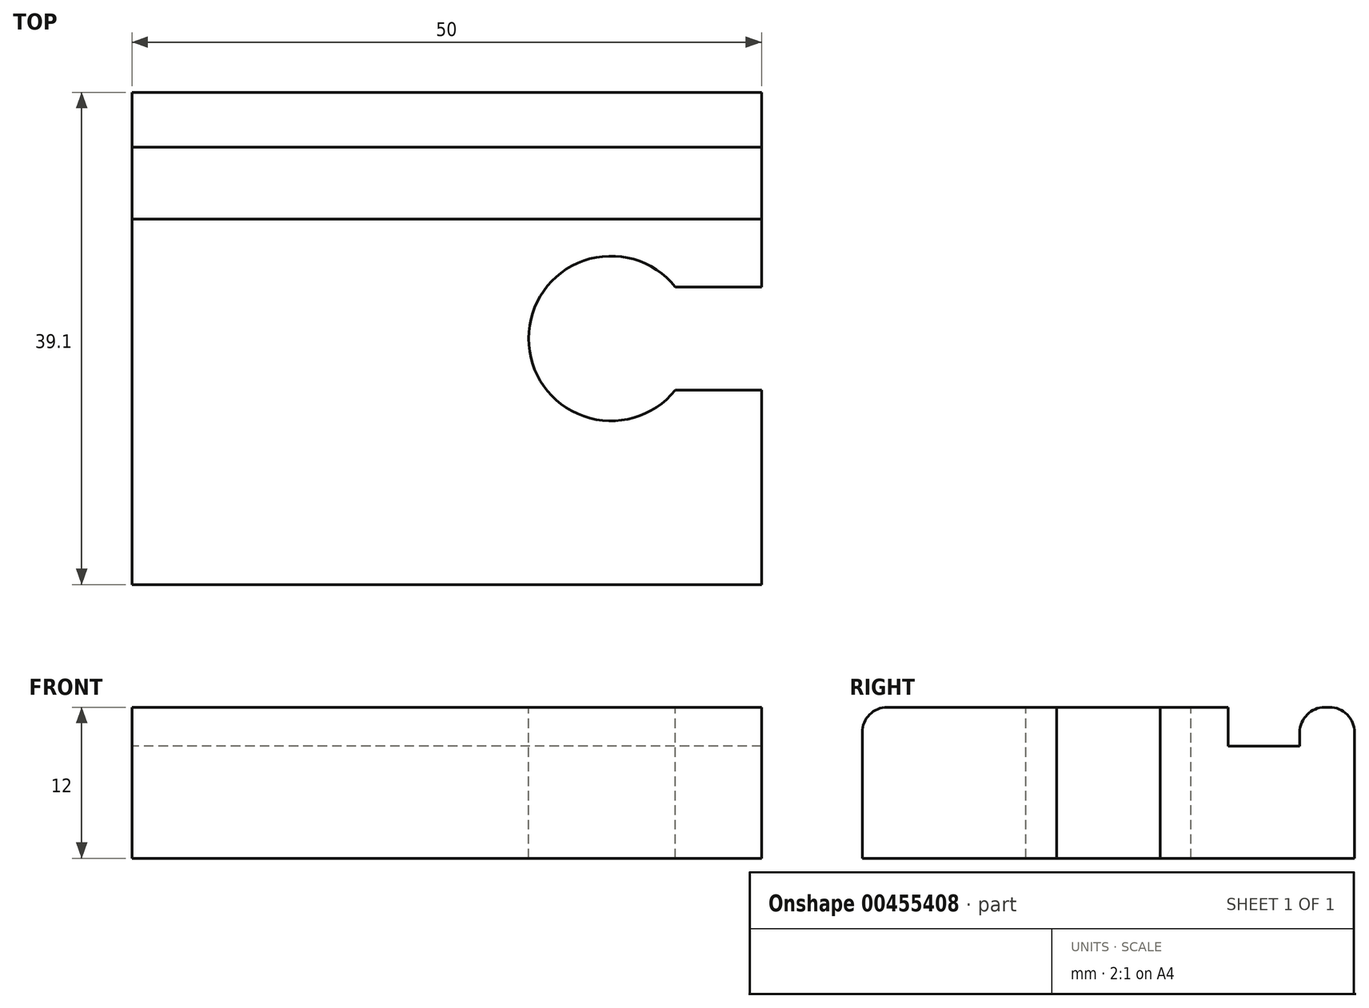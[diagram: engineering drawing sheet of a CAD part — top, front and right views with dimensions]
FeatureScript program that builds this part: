
annotation { "Feature Type Name" : "Feature", "Feature Type Description" : "" }
export const myFeature = defineFeature(function(context is Context, id is Id, definition is map)
    precondition{}
    {
        {
            var Q0;
            Q0=qCreatedBy(makeId("Top.planeOp"),FACE);
            var sketch = newSketch(context, id + "F0", { "sketchPlane" : qUnion([Q0])});
            skLineSegment(sketch, "E0.bottom", {"start": v(-25, 19.55) * mm, "end": v(25, 19.55) * mm});
            skLineSegment(sketch, "E0.top", {"start": v(-25, -19.55) * mm, "end": v(25, -19.55) * mm});
            skLineSegment(sketch, "E0.left", {"start": v(-25, 19.55) * mm, "end": v(-25, -19.55) * mm});
            skLineSegment(sketch, "E0.right", {"start": v(25, 19.55) * mm, "end": v(25, -19.55) * mm});
            skLineSegment(sketch, "E1", {"start": v(25, 0) * mm, "end": v(-25, 0) * mm, "construction": true});
            skLineSegment(sketch, "E2", {"start": v(0, 19.55) * mm, "end": v(0, -19.55) * mm, "construction": true});
            skSolve(sketch);
        }
        {
            var Q0;
            Q0=makeQuery(id+"F0.imprint","IMPRINT",FACE,{"disambiguationData":[TD([[makeQuery(id+"F0.imprint","IMPRINT",EDGE,{"derivedFrom":sQuery(id+"F0.wireOp",EDGE,"E0.bottom")}),-1.0]])]});
            extrude(context, id + "F1", {"entities" : qUnion([Q0]), "endBound" : BoundingType.SYMMETRIC, "depth" : 12 * mm});
        }
        {
            var Q0;
            Q0=makeQuery(id+"F1.opExtrude","CAP_FACE",FACE,{"disambiguationData":[OSD([sQuery(id+"F0.wireOp",EDGE,"E0.bottom"),sQuery(id+"F0.wireOp",EDGE,"E0.top"),sQuery(id+"F0.wireOp",EDGE,"E0.left"),sQuery(id+"F0.wireOp",EDGE,"E0.right")])],"isStart":false});
            var sketch = newSketch(context, id + "F2", { "sketchPlane" : qUnion([Q0])});
            skLineSegment(sketch, "E3", {"start": v(25, 0) * mm, "end": v(25, 4.1) * mm});
            skLineSegment(sketch, "E4", {"start": v(25, 4.1) * mm, "end": v(18.16, 4.1) * mm});
            skArc(sketch, "E5", {"start": v(18.16, 4.1) * mm, "mid": v(6.5, 0) * mm, "end": v(18.16, -4.1) * mm});
            skLineSegment(sketch, "E6", {"start": v(25, 0) * mm, "end": v(25, -4.1) * mm});
            skLineSegment(sketch, "E7", {"start": v(25, -4.1) * mm, "end": v(18.16, -4.1) * mm});
            skLineSegment(sketch, "E8", {"start": v(25, 15.2) * mm, "end": v(-25, 15.2) * mm});
            skLineSegment(sketch, "E9", {"start": v(-25, 15.2) * mm, "end": v(-25, 9.5) * mm});
            skLineSegment(sketch, "E10", {"start": v(-25, 9.5) * mm, "end": v(25, 9.5) * mm});
            skLineSegment(sketch, "E11", {"start": v(25, 9.5) * mm, "end": v(25, 15.2) * mm});
            skSolve(sketch);
        }
        {
            var Q0;
            Q0=makeQuery(id+"F2.imprint","IMPRINT",FACE,{"disambiguationData":[TD([[makeQuery(id+"F2.imprint","IMPRINT",EDGE,{"derivedFrom":sQuery(id+"F2.wireOp",EDGE,"E8")}),1.0]])]});
            extrude(context, id + "F3", {"entities" : qUnion([Q0]), "operationType" : NewBodyOperationType.REMOVE, "oppositeDirection" : true, "depth" : 3.1 * mm});
        }
        {
            var Q0;
            Q0=makeQuery(id+"F2.imprint","IMPRINT",FACE,{"disambiguationData":[TD([[makeQuery(id+"F2.imprint","IMPRINT",EDGE,{"derivedFrom":sQuery(id+"F2.wireOp",EDGE,"E3")}),-1.0]])]});
            extrude(context, id + "F4", {"entities" : qUnion([Q0]), "operationType" : NewBodyOperationType.REMOVE, "endBound" : BoundingType.UP_TO_NEXT, "oppositeDirection" : true, "depth" : 25 * mm});
        }
        {
            var Q0;
            Q0=makeQuery(id+"F1.opExtrude","CAP_EDGE",EDGE,{"disambiguationData":[OSD([sQuery(id+"F0.wireOp",EDGE,"E0.top")])],"isStart":false});
            var Q1;
            Q1=makeQuery(id+"FonFhPnYcRC40cm_1.boolean.opBoolean","COPY",EDGE,{"derivedFrom":makeQuery(id+"FonFhPnYcRC40cm_1.opExtrude","CAP_EDGE",EDGE,{"disambiguationData":[OSD([sQuery(id+"FOFUt4QlGWim4YD_1.1.FOkan6ajuEyo38N_1.1.F2.wireOp",EDGE,"E8")])],"isStart":true})});
            var Q2;
            Q2=makeQuery(id+"F3.boolean.opBoolean","COPY",EDGE,{"derivedFrom":makeQuery(id+"F3.opExtrude","CAP_EDGE",EDGE,{"disambiguationData":[OSD([sQuery(id+"F2.wireOp",EDGE,"E8")])],"isStart":true})});
            var Q3;
            Q3=makeQuery(id+"F1.opExtrude","CAP_EDGE",EDGE,{"disambiguationData":[OSD([sQuery(id+"F0.wireOp",EDGE,"E0.bottom")])],"isStart":false});
            fillet(context, id + "F5", {"entities" : qUnion([Q0, Q1, Q2, Q3]), "radius" : 2 * mm, "tangentPropagation" : true, "allowEdgeOverflow" : false});
        }
    });
